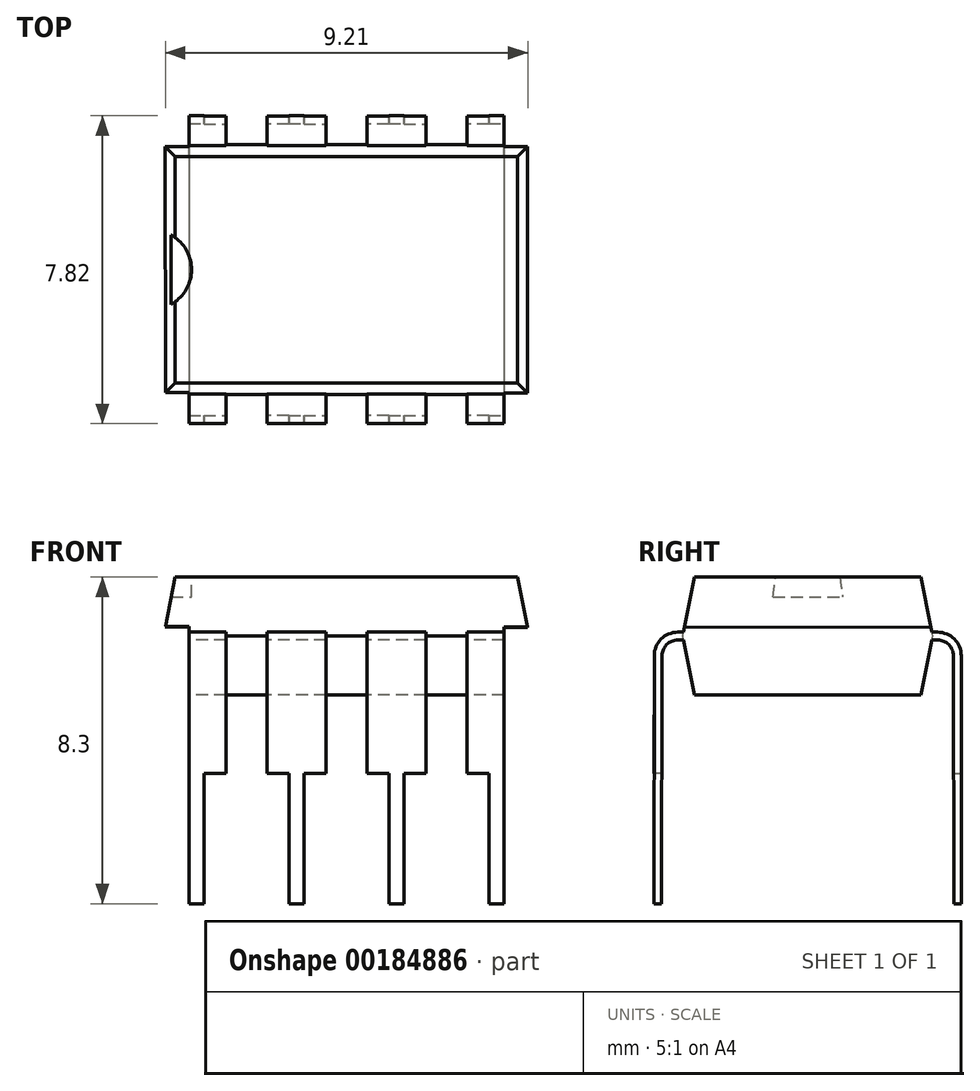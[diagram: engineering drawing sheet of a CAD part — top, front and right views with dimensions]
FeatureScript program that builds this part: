
annotation { "Feature Type Name" : "Feature", "Feature Type Description" : "" }
export const myFeature = defineFeature(function(context is Context, id is Id, definition is map)
    precondition{}
    {
        {
            var Q0;
            Q0=qCreatedBy(makeId("Top.planeOp"),FACE);
            cPlane(context, id + "F0", {"entities" : qUnion([Q0]), "cplaneType" : CPlaneType.OFFSET, "offset" : 2 * mm, "width" : 150 * mm, "height" : 150 * mm});
        }
        {
            var Q0;
            Q0=qCreatedBy(id+"F0.planeOp",FACE);
            cPlane(context, id + "F1", {"entities" : qUnion([Q0]), "cplaneType" : CPlaneType.OFFSET, "offset" : 1.5 * mm, "width" : 150 * mm, "height" : 150 * mm});
        }
        {
            var Q0;
            Q0=qCreatedBy(id+"F1.planeOp",FACE);
            cPlane(context, id + "F2", {"entities" : qUnion([Q0]), "cplaneType" : CPlaneType.OFFSET, "offset" : 1.5 * mm, "width" : 150 * mm, "height" : 150 * mm});
        }
        {
            var Q0;
            Q0=qCreatedBy(id+"F1.planeOp",FACE);
            var sketch = newSketch(context, id + "F3", { "sketchPlane" : qUnion([Q0])});
            skLineSegment(sketch, "E0.bottom", {"start": v(4.65, 3.17) * mm, "end": v(-4.65, 3.17) * mm});
            skLineSegment(sketch, "E0.top", {"start": v(4.65, -3.17) * mm, "end": v(-4.65, -3.17) * mm});
            skLineSegment(sketch, "E0.left", {"start": v(4.65, 3.17) * mm, "end": v(4.65, -3.17) * mm});
            skLineSegment(sketch, "E0.right", {"start": v(-4.65, 3.17) * mm, "end": v(-4.65, -3.17) * mm});
            skPoint(sketch, "E0.middle", {"position": v(0, 0) * mm});
            skSolve(sketch);
        }
        {
            var Q0;
            Q0=qCreatedBy(id+"F0.planeOp",FACE);
            var sketch = newSketch(context, id + "F4", { "sketchPlane" : qUnion([Q0])});
            skLineSegment(sketch, "E1.0", {"start": v(4.35, 2.88) * mm, "end": v(-4.35, 2.88) * mm});
            skLineSegment(sketch, "E1.1", {"start": v(4.35, 2.88) * mm, "end": v(4.35, -2.88) * mm});
            skLineSegment(sketch, "E1.2", {"start": v(4.35, -2.88) * mm, "end": v(-4.35, -2.88) * mm});
            skLineSegment(sketch, "E1.3", {"start": v(-4.35, 2.88) * mm, "end": v(-4.35, -2.87) * mm});
            skSolve(sketch);
        }
        {
            var Q0;
            Q0=qCreatedBy(id+"F2.planeOp",FACE);
            var sketch = newSketch(context, id + "F5", { "sketchPlane" : qUnion([Q0])});
            skLineSegment(sketch, "E2.0", {"start": v(4.35, 2.88) * mm, "end": v(-4.35, 2.88) * mm});
            skLineSegment(sketch, "E2.1", {"start": v(4.35, 2.88) * mm, "end": v(4.35, -2.88) * mm});
            skLineSegment(sketch, "E2.2", {"start": v(4.35, -2.88) * mm, "end": v(-4.35, -2.88) * mm});
            skLineSegment(sketch, "E2.3", {"start": v(-4.35, 2.88) * mm, "end": v(-4.35, -2.87) * mm});
            skSolve(sketch);
        }
        {
            var Q0;
            Q0=qSketchRegion(id+"F4",true);
            var Q1;
            Q1=qSketchRegion(id+"F3",true);
            loft(context, id + "F6", {"sheetProfilesArray" : [{ "sheetProfileEntities" : qUnion([Q0]) }, { "sheetProfileEntities" : qUnion([Q1]) }]});
        }
        {
            var Q1;
            Q1=qSketchRegion(id+"F3",true);
            var Q2;
            Q2=qSketchRegion(id+"F5",true);
            loft(context, id + "F7", {"operationType" : NewBodyOperationType.ADD, "sheetProfilesArray" : [{ "sheetProfileEntities" : qUnion([Q1]) }, { "sheetProfileEntities" : qUnion([Q2]) }]});
        }
        {
            var Q0;
            Q0=makeQuery(id+"F7.opLoft","CAP_FACE",FACE,{"disambiguationData":[OSD([makeQuery(id+"F5.imprint","IMPRINT",FACE,{"disambiguationData":[TD([[makeQuery(id+"F5.imprint","IMPRINT",EDGE,{"derivedFrom":sQuery(id+"F5.wireOp",EDGE,"E2.0")}),1.0]])]})])],"isStart":true});
            var sketch = newSketch(context, id + "F8", { "sketchPlane" : qUnion([Q0])});
            skArc(sketch, "E3", {"start": v(-4.5, -0.91) * mm, "mid": v(-3.94, 0) * mm, "end": v(-4.5, 0.91) * mm});
            skLineSegment(sketch, "E4", {"start": v(-4.5, 0.91) * mm, "end": v(-4.5, -0.91) * mm});
            skSolve(sketch);
        }
        {
            var Q0;
            Q0=qSketchRegion(id+"F8",true);
            extrude(context, id + "F9", {"entities" : qUnion([Q0]), "operationType" : NewBodyOperationType.REMOVE, "oppositeDirection" : true, "depth" : 0.5 * mm});
        }
        {
            var Q0;
            Q0=qCreatedBy(makeId("Right.planeOp"),FACE);
            var sketch = newSketch(context, id + "F10", { "sketchPlane" : qUnion([Q0])});
            skLineSegment(sketch, "E5", {"start": v(-2.03, 3.5) * mm, "end": v(-3.3, 3.5) * mm});
            skLineSegment(sketch, "E6", {"start": v(-3.8, 3) * mm, "end": v(-3.81, -3.3) * mm});
            skPoint(sketch, "E7.visualSharp", {"position": v(-3.8, 3.5) * mm});
            skArc(sketch, "E7.filletArc", {"start": v(-3.3, 3.5) * mm, "mid": v(-3.65, 3.35) * mm, "end": v(-3.8, 3) * mm});
            skSolve(sketch);
        }
        {
            var Q0;
            Q0=sQuery(id+"F10.wireOp",VERTEX,"E6.end");
            var Q1;
            Q1=sQuery(id+"F10.wireOp",EDGE,"E6");
            cPlane(context, id + "F11", {"entities" : qUnion([Q0, Q1]), "cplaneType" : CPlaneType.CURVE_POINT, "offset" : 25 * mm, "width" : 150 * mm, "height" : 150 * mm});
        }
        {
            var Q0;
            Q0=qCreatedBy(id+"F11.planeOp",FACE);
            var sketch = newSketch(context, id + "F12", { "sketchPlane" : qUnion([Q0])});
            skLineSegment(sketch, "E8.bottom", {"start": v(-0.75, 3.9) * mm, "end": v(0.75, 3.9) * mm});
            skLineSegment(sketch, "E8.top", {"start": v(-0.75, 3.7) * mm, "end": v(0.75, 3.7) * mm});
            skLineSegment(sketch, "E8.left", {"start": v(-0.75, 3.9) * mm, "end": v(-0.75, 3.7) * mm});
            skLineSegment(sketch, "E8.right", {"start": v(0.75, 3.9) * mm, "end": v(0.75, 3.7) * mm});
            skPoint(sketch, "E8.middle", {"position": v(0, 3.8) * mm});
            skSolve(sketch);
        }
        {
            var Q0;
            Q0=qSketchRegion(id+"F12",true);
            var Q1;
            Q1=qConstructionFilter(qBodyType(qCreatedBy(id+"F10",EDGE),BodyType.WIRE),ConstructionObject.NO);
            sweep(context, id + "F13", {"profiles" : qUnion([Q0]), "path" : qUnion([Q1])});
        }
        {
            var Q0;
            Q0=makeQuery(id+"F13.opSweep","SWEPT_FACE",FACE,{"disambiguationData":[OSD([sQuery(id+"F10.wireOp",EDGE,"E6"),sQuery(id+"F12.wireOp",EDGE,"E8.bottom")])]});
            var sketch = newSketch(context, id + "F14", { "sketchPlane" : qUnion([Q0])});
            skLineSegment(sketch, "E9.bottom", {"start": v(-0.8, 0) * mm, "end": v(-0.19, 0) * mm});
            skLineSegment(sketch, "E9.top", {"start": v(-0.8, -4.04) * mm, "end": v(-0.19, -4.04) * mm});
            skLineSegment(sketch, "E9.left", {"start": v(-0.8, 0) * mm, "end": v(-0.8, -4.04) * mm});
            skLineSegment(sketch, "E9.right", {"start": v(-0.19, 0) * mm, "end": v(-0.19, -4.04) * mm});
            skLineSegment(sketch, "E10", {"start": v(0, -0.14) * mm, "end": v(0, -0.8) * mm});
            skLineSegment(sketch, "E11.MirrorCS", {"start": v(0.8, 0) * mm, "end": v(0.19, 0) * mm});
            skLineSegment(sketch, "E12.MirrorCS", {"start": v(0.8, -4.04) * mm, "end": v(0.19, -4.04) * mm});
            skLineSegment(sketch, "E13.MirrorCS", {"start": v(0.19, 0) * mm, "end": v(0.19, -4.04) * mm});
            skLineSegment(sketch, "E14.MirrorCS", {"start": v(0.8, 0) * mm, "end": v(0.8, -4.04) * mm});
            skSolve(sketch);
        }
        {
            var Q0;
            Q0=qSketchRegion(id+"F14",true);
            extrude(context, id + "F15", {"entities" : qUnion([Q0]), "operationType" : NewBodyOperationType.REMOVE, "oppositeDirection" : true, "depth" : 25 * mm});
        }
        {
            var Q0;
            Q0=makeQuery(id+"F13.opSweep","SWEPT_BODY",BODY,{"disambiguationData":[OSD([sQuery(id+"F10.wireOp",EDGE,"E6"),sQuery(id+"F12.wireOp",EDGE,"E8.bottom"),sQuery(id+"F12.wireOp",EDGE,"E8.top"),sQuery(id+"F12.wireOp",EDGE,"E8.left"),sQuery(id+"F12.wireOp",EDGE,"E8.right")])]});
            transform(context, id + "F16", {"entities" : qUnion([Q0]), "transformType" : TransformType.TRANSLATION_3D, "dx" : -1.27 * mm, "dy" : 0 * mm, "dz" : 0 * mm, "makeCopy" : false});
        }
        {
            var Q0;
            Q0=makeQuery(id+"F13.opSweep","SWEPT_BODY",BODY,{"disambiguationData":[OSD([sQuery(id+"F10.wireOp",EDGE,"E6"),sQuery(id+"F12.wireOp",EDGE,"E8.bottom"),sQuery(id+"F12.wireOp",EDGE,"E8.top"),sQuery(id+"F12.wireOp",EDGE,"E8.left"),sQuery(id+"F12.wireOp",EDGE,"E8.right")])]});
            transform(context, id + "F17", {"entities" : qUnion([Q0]), "transformType" : TransformType.TRANSLATION_3D, "dx" : 2.54 * mm, "dy" : 0 * mm, "dz" : 0 * mm, "makeCopy" : true});
        }
        {
            var Q0;
            Q0=makeQuery(id+"F13.opSweep","SWEPT_BODY",BODY,{"disambiguationData":[OSD([sQuery(id+"F10.wireOp",EDGE,"E6"),sQuery(id+"F12.wireOp",EDGE,"E8.bottom"),sQuery(id+"F12.wireOp",EDGE,"E8.top"),sQuery(id+"F12.wireOp",EDGE,"E8.left"),sQuery(id+"F12.wireOp",EDGE,"E8.right")])]});
            transform(context, id + "F18", {"entities" : qUnion([Q0]), "transformType" : TransformType.TRANSLATION_3D, "dx" : -2.54 * mm, "dy" : 0 * mm, "dz" : 0 * mm, "makeCopy" : true});
        }
        {
            var Q0;
            Q0=makeQuery(id+"F17.opPattern","COPY",BODY,{"derivedFrom":makeQuery(id+"F13.opSweep","SWEPT_BODY",BODY,{"disambiguationData":[OSD([sQuery(id+"F10.wireOp",EDGE,"E6"),sQuery(id+"F12.wireOp",EDGE,"E8.bottom"),sQuery(id+"F12.wireOp",EDGE,"E8.top"),sQuery(id+"F12.wireOp",EDGE,"E8.left"),sQuery(id+"F12.wireOp",EDGE,"E8.right")])]}),"instanceName":"1"});
            transform(context, id + "F19", {"entities" : qUnion([Q0]), "transformType" : TransformType.TRANSLATION_3D, "dx" : 2.54 * mm, "dy" : 0 * mm, "dz" : 0 * mm, "makeCopy" : true});
        }
        {
            var Q0;
            Q0=makeQuery(id+"F18.opPattern","COPY",FACE,{"derivedFrom":makeQuery(id+"F13.opSweep","SWEPT_FACE",FACE,{"disambiguationData":[OSD([sQuery(id+"F10.wireOp",EDGE,"E6"),sQuery(id+"F12.wireOp",EDGE,"E8.bottom")])]}),"instanceName":"1"});
            var sketch = newSketch(context, id + "F20", { "sketchPlane" : qUnion([Q0])});
            skLineSegment(sketch, "E15.bottom", {"start": v(-5.3, 3.74) * mm, "end": v(-4, 3.74) * mm});
            skLineSegment(sketch, "E15.top", {"start": v(-5.3, -0.75) * mm, "end": v(-4, -0.75) * mm});
            skLineSegment(sketch, "E15.left", {"start": v(-5.3, 3.74) * mm, "end": v(-5.3, -0.75) * mm});
            skLineSegment(sketch, "E15.right", {"start": v(-4, 3.74) * mm, "end": v(-4, -0.75) * mm});
            skSolve(sketch);
        }
        {
            var Q0;
            Q0=qSketchRegion(id+"F20",true);
            extrude(context, id + "F21", {"entities" : qUnion([Q0]), "operationType" : NewBodyOperationType.REMOVE, "oppositeDirection" : true, "depth" : 25 * mm});
        }
        {
            var Q0;
            Q0=makeQuery(id+"F19.opPattern","COPY",FACE,{"derivedFrom":makeQuery(id+"F17.opPattern","COPY",FACE,{"derivedFrom":makeQuery(id+"F13.opSweep","SWEPT_FACE",FACE,{"disambiguationData":[OSD([sQuery(id+"F10.wireOp",EDGE,"E6"),sQuery(id+"F12.wireOp",EDGE,"E8.bottom")])]}),"instanceName":"1"}),"instanceName":"1"});
            var sketch = newSketch(context, id + "F22", { "sketchPlane" : qUnion([Q0])});
            skLineSegment(sketch, "E16.bottom", {"start": v(5.51, 3.73) * mm, "end": v(4, 3.73) * mm});
            skLineSegment(sketch, "E16.top", {"start": v(5.51, -0.79) * mm, "end": v(4, -0.79) * mm});
            skLineSegment(sketch, "E16.left", {"start": v(5.51, 3.73) * mm, "end": v(5.51, -0.79) * mm});
            skLineSegment(sketch, "E16.right", {"start": v(4, 3.73) * mm, "end": v(4, -0.79) * mm});
            skSolve(sketch);
        }
        {
            var Q0;
            Q0=qSketchRegion(id+"F22",true);
            extrude(context, id + "F23", {"entities" : qUnion([Q0]), "operationType" : NewBodyOperationType.REMOVE, "oppositeDirection" : true, "depth" : 25 * mm});
        }
        {
            var Q0;
            Q0=makeQuery(id+"F18.opPattern","COPY",BODY,{"derivedFrom":makeQuery(id+"F13.opSweep","SWEPT_BODY",BODY,{"disambiguationData":[OSD([sQuery(id+"F10.wireOp",EDGE,"E6"),sQuery(id+"F12.wireOp",EDGE,"E8.bottom"),sQuery(id+"F12.wireOp",EDGE,"E8.top"),sQuery(id+"F12.wireOp",EDGE,"E8.left"),sQuery(id+"F12.wireOp",EDGE,"E8.right")])]}),"instanceName":"1"});
            var Q1;
            Q1=makeQuery(id+"F13.opSweep","SWEPT_BODY",BODY,{"disambiguationData":[OSD([sQuery(id+"F10.wireOp",EDGE,"E6"),sQuery(id+"F12.wireOp",EDGE,"E8.bottom"),sQuery(id+"F12.wireOp",EDGE,"E8.top"),sQuery(id+"F12.wireOp",EDGE,"E8.left"),sQuery(id+"F12.wireOp",EDGE,"E8.right")])]});
            var Q2;
            Q2=makeQuery(id+"F17.opPattern","COPY",BODY,{"derivedFrom":makeQuery(id+"F13.opSweep","SWEPT_BODY",BODY,{"disambiguationData":[OSD([sQuery(id+"F10.wireOp",EDGE,"E6"),sQuery(id+"F12.wireOp",EDGE,"E8.bottom"),sQuery(id+"F12.wireOp",EDGE,"E8.top"),sQuery(id+"F12.wireOp",EDGE,"E8.left"),sQuery(id+"F12.wireOp",EDGE,"E8.right")])]}),"instanceName":"1"});
            var Q3;
            Q3=makeQuery(id+"F19.opPattern","COPY",BODY,{"derivedFrom":makeQuery(id+"F17.opPattern","COPY",BODY,{"derivedFrom":makeQuery(id+"F13.opSweep","SWEPT_BODY",BODY,{"disambiguationData":[OSD([sQuery(id+"F10.wireOp",EDGE,"E6"),sQuery(id+"F12.wireOp",EDGE,"E8.bottom"),sQuery(id+"F12.wireOp",EDGE,"E8.top"),sQuery(id+"F12.wireOp",EDGE,"E8.left"),sQuery(id+"F12.wireOp",EDGE,"E8.right")])]}),"instanceName":"1"}),"instanceName":"1"});
            var Q4;
            Q4=qCreatedBy(makeId("Front.planeOp"),FACE);
            mirror(context, id + "F24", {"operationType" : NewBodyOperationType.ADD, "entities" : qUnion([Q0, Q1, Q2, Q3]), "mirrorPlane" : qUnion([Q4])});
        }
    });
